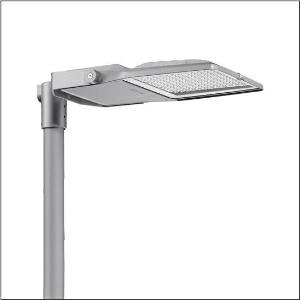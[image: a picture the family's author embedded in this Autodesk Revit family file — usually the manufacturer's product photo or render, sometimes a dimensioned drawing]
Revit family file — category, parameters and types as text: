
# Revit family: floodlight_fl_21_iq_midi___pl52_5xa7781e4d3a_f0c1
name_source: partatom
category: Lighting Fixtures
units: mm (PartAtom-declared; Revit-internal decimal feet)

## family parameters
Cut with Voids When Loaded = No
Host = Face
Light Source = No
Part Type = Normal
Room Calculation Point = No
Round Connector Dimension = Use Diameter
Shared = No

## types (1)
- --- (1 x LED, 28010 lm, 208.1 W, 4000K)
    Apparent Load = 208 VA
    CIE Flux Codes = 26 60 98 100 100
    Color Rendering = 70
    Color Temperature = 4000K
    Default Elevation = 1800 mm
    Description = Floodlight FL 21 iQ midi, floodlight, primary light control with lens, of PMMA, primary optical cover: protective disc, of toughened safety glass, transparent, light distribution: PL52, light emission: direct distribution, installation type: surface-mounted, LED, High Power LED, rated luminous flux: 28.010lm, luminous efficacy: 135lm/W, light colour: 740, colour temperature: 4000K, control gear: ECG iQ, control: optimised constant luminous flux control (CLO 2.0), Desk-Remote (wireless, voltage-free reading and setting of iQ features in the workshop via application-optimized NFC function/RFID function), Light-Fading, Smart-Wire, Night-Set, Lumen-Switch, Temp-Guard, Auto-Match, with terminal, 6-pole, mains connection: 220..240V, AC, 50/60Hz, start of lifetime: 208W, end of service life: 227W, reduction: 90W, luminaire housing, of diecast aluminium, powder-coated, Siteco® metallic grey (DB 702S), corrosivity category C5 mid according to DIN EN ISO 12944, sealing non-destructively replaceable, please order mast flange separately, mast bracket, of steel, galvanised, powder-coated, Siteco® metallic grey (DB 702S), protection rating (complete): IP66, insulation class (complete): insulation class II (safety insulation), certification: CE, protection symbol: D, impact resistance: IK08, permissible operating ambient temperature: -40..+40°C, permissible operating ambient temperature for outdoor applications: -40..+50°C, standard: DIN EN 12944, LABS conformity tested according to VDMA 24364:2018-05, packaging unit: 1 piece

Light Distribution: PL52
    Height = 76 mm
    Lamp = 1 x LED
    Lamp Light Flux = 28010 lm
    Lamp Power = 208.1 W
    Lamp count = 1
    Length = 657 mm
    Luminous efficacy = 135 lm/W
    Manufacturer = Siteco
    ModVariant = No
    Model = 5XA7781E4D3A
    Number of Poles = 1
    OnlyDefault = Yes
    Power Factor = 1
    Product Name = Floodlight FL 21 iQ midi | PL52
    Product group = floodlight | pylon annexe
    ProductGroupID = 6200
    Protection Class = Protection class II
    Protection Degree = IP 66
    RLX_Detail_Level = 1
    RLX_Emergency_Light_Flux = 0 lm
    RLX_Emergency_Type = 0
    RLX_Emergency_Type_DB = No
    RlxData = <blob elided: 153917 chars, md5=56284c4a>
    Socket = socket
    Standby Power = 0 W
    System Light Flux = 28010 lm
    System Power = 208 W
    Type Comments = factory setting: luminous flux: 100 % | dim-lin: 254 | 710 mA
    Type Image = l_1007123.jpg
    URL = http://relux.com
    VarID = @adj_036327
    Voltage = 0 V
    Weight = 0.00 kg
    Width = 442 mm

## geometry (parser evidence)
native form markers: Blend x4, Sweep x11
no freeform markers — native parametric forms only
